# Revit family: URA Eclairage de Séurité_URAPROOF V LSC
name_source: partatom
category: Luminaires
units: mm (PartAtom-declared; Revit-internal decimal feet)

## family parameters
Conserver l'orientation des annotations = Non
Cote de connecteur circulaire = Utiliser le diamètre
Couper avec des vides une fois chargée = Non
Hôte = Face
Partagée = Non
Repère de localisation dans la pièce = Non
Source d'éclairage = Non
Type d'élément = Normal

## types (4) — shared parameters
Adressable = Non
Alimentation de secours = Centralisé (source centrale)
Classe ETIM = EC001957-Luminaire d'éclairage de sécurité
Classe de protection = II
Conditions Générale d'Utilisation = https://export.legrand.com
Consommation en veille = 0 A
Couleur = Gris
Elévation par défaut = 2300 mm
Entraxe de fixation horizontale = 150
Fabricant = URA
Flux lumineux en veille = 3 lm
Fréquence = 50/60 Hz
Hauteur = 62 mm  [stored 0.203412 ft]
IK = 10
IP = 66
Largeur = 125 mm  [stored 0.410105 ft]
Longueur = 225 mm  [stored 0.738189 ft]
Matière = Plastique
Mode de pose = Montage en saillie (mur)
Objet Connecté = Non
Pictogramme Inclus = Oui
Système de contrôle = sans
Temperature d'utilisation MIN-MAX = -5°C +35°C
Type de commutation = Permanent
Type de connexion = Raccordement à vis
Type de pictogramme = Feuillet/plaque inséré(e)
URL = www.ura.fr
capacité des bornes = 1,5-2,5 mm2
source lumineuse = LED non interchangeable

## per-type parameters (varying)
| type | Ambiance | Code EAN | Description Produit | Evac | Flux lumineux utile | Fonction | Puissance du système | Référence / Modèle | Tension |
| .1-LSC Evacuation 48-220V - 45 lm | Non | 3613400170654 | LSC URAPROOF V EVACUATION 48-220VDC/230VAC 45LM IP66 IK10 | Oui | 45 lm | Éclairage d'évacuation | 1 W | UR127514V | 48-230 VAC/DC |
| .2-LSC Evacuation 24V - 45 lm | Non | 3613400170678 | LSC URAPROOF V EVACUATION 24VDC 45LM IP66 IK10 | Oui | 45 lm | Éclairage d'évacuation | 2 W | UR127515V | 24 VDC |
| .3-LSC Ambiance 48-220V - 400 lm | Oui | 3613400170586 | LSC URAPROOF V AMBIANCE 48-220VDC/230VAC 400LM IP66 IK10 | Non | 400 lm | Éclairage d'ambiance (anti-panique) | 6 W | UR127524V | 48-230 VAC/DC |
| .4-LSC Ambiance 24V - 400 lm | Oui | 3613400170609 | LSC URAPROOF V AMBIANCE 24VDC 400LM IP66 IK10 | Non | 400 lm | Éclairage d'ambiance (anti-panique) | 4 W | UR127525V | 24 VDC |

note: [stored X ft] marks values corroborated as IEEE doubles in the binary element streams (Revit-internal decimal feet)
